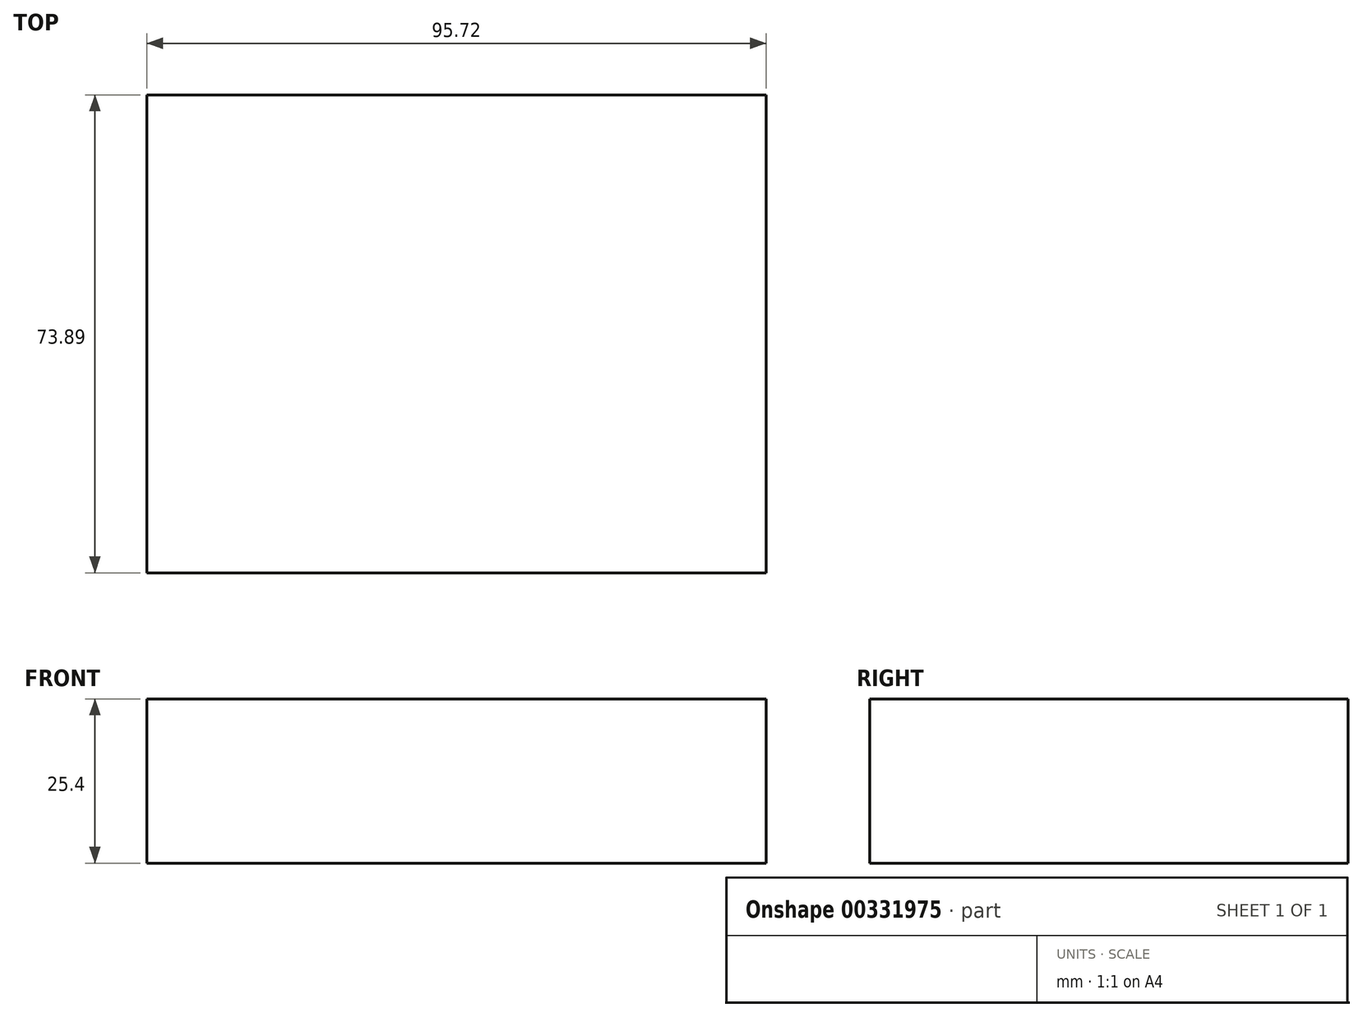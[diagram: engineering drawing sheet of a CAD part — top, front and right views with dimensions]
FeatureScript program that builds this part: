
annotation { "Feature Type Name" : "Feature", "Feature Type Description" : "" }
export const myFeature = defineFeature(function(context is Context, id is Id, definition is map)
    precondition{}
    {
        {
            var Q0;
            Q0=qCreatedBy(makeId("Top.planeOp"),FACE);
            var sketch = newSketch(context, id + "F0", { "sketchPlane" : qUnion([Q0])});
            skLineSegment(sketch, "E0.bottom", {"start": v(-84.26, 27.45) * mm, "end": v(11.46, 27.45) * mm});
            skLineSegment(sketch, "E0.top", {"start": v(-84.26, -46.44) * mm, "end": v(11.46, -46.44) * mm});
            skLineSegment(sketch, "E0.left", {"start": v(-84.26, 27.45) * mm, "end": v(-84.26, -46.44) * mm});
            skLineSegment(sketch, "E0.right", {"start": v(11.46, 27.45) * mm, "end": v(11.46, -46.44) * mm});
            skSolve(sketch);
        }
        {
            var Q0;
            Q0 = qSketchRegion(id + "F0", true);
            extrude(context, id + "F1", {"entities" : qUnion([Q0]), "endBound" : BoundingType.SYMMETRIC, "depth" : 25.4 * mm});
        }
    });
